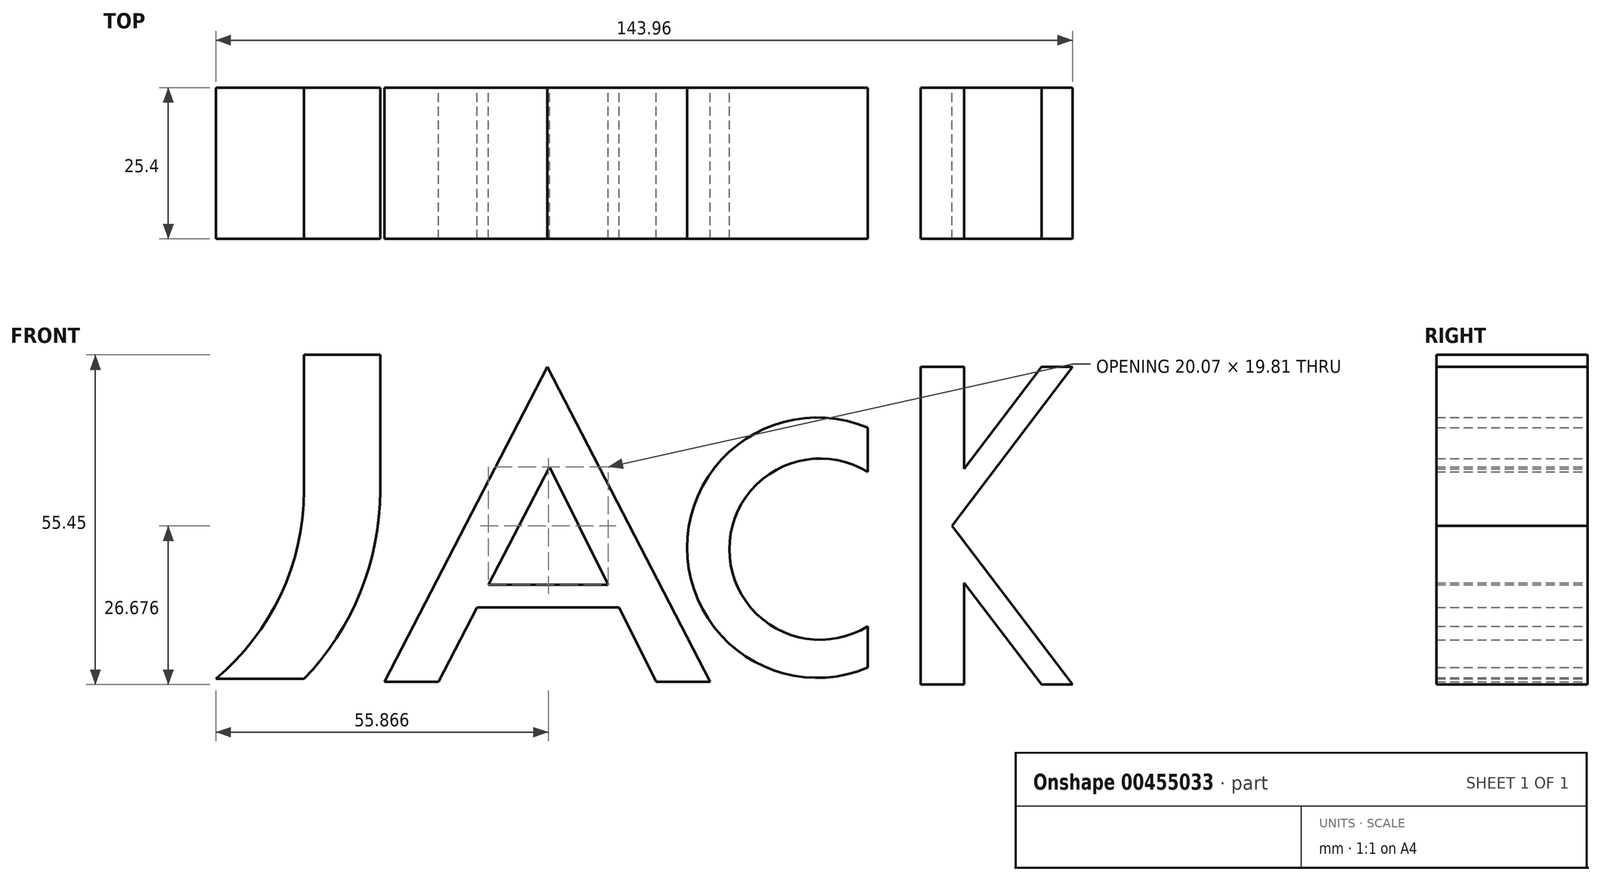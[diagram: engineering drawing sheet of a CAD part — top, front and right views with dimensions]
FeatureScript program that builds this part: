
annotation { "Feature Type Name" : "Feature", "Feature Type Description" : "" }
export const myFeature = defineFeature(function(context is Context, id is Id, definition is map)
    precondition{}
    {
        {
            var Q0;
            Q0=qCreatedBy(makeId("Front.planeOp"),FACE);
            var sketch = newSketch(context, id + "F0", { "sketchPlane" : qUnion([Q0])});
            skLineSegment(sketch, "E0", {"start": v(-52.69, 32.43) * mm, "end": v(-39.89, 32.43) * mm});
            skLineSegment(sketch, "E1", {"start": v(-39.89, 32.43) * mm, "end": v(-39.89, 9.58) * mm});
            skLineSegment(sketch, "E2", {"start": v(-39.89, 9.58) * mm, "end": v(-39.89, 32.43) * mm});
            skLineSegment(sketch, "E3", {"start": v(-52.69, 32.43) * mm, "end": v(-52.69, 9.58) * mm});
            skArc(sketch, "E4", {"start": v(-52.69, -22.05) * mm, "mid": v(-43.2, -7.48) * mm, "end": v(-39.89, 9.58) * mm});
            skPoint(sketch, "E4.startSnap0", {"position": v(-52.69, 21) * mm});
            skArc(sketch, "E5", {"start": v(-67.5, -22.05) * mm, "mid": v(-56.58, -7.88) * mm, "end": v(-52.69, 9.58) * mm});
            skLineSegment(sketch, "E6", {"start": v(-67.5, -22.05) * mm, "end": v(-52.69, -22.05) * mm});
            skLineSegment(sketch, "E7", {"start": v(-39.13, -22.55) * mm, "end": v(-11.76, 30.42) * mm});
            skLineSegment(sketch, "E8", {"start": v(-11.76, 30.42) * mm, "end": v(15.6, -22.55) * mm});
            skLineSegment(sketch, "E9", {"start": v(-39.13, -22.55) * mm, "end": v(-30.1, -22.55) * mm});
            skLineSegment(sketch, "E10", {"start": v(-30.1, -22.55) * mm, "end": v(-23.64, -10.06) * mm});
            skLineSegment(sketch, "E11", {"start": v(15.6, -22.55) * mm, "end": v(6.5, -22.55) * mm});
            skLineSegment(sketch, "E12", {"start": v(-11.44, 13.56) * mm, "end": v(-1.6, -6.25) * mm});
            skLineSegment(sketch, "E13", {"start": v(-23.64, -10.06) * mm, "end": v(0, -10.06) * mm});
            skLineSegment(sketch, "E14", {"start": v(0, -10.06) * mm, "end": v(-23.64, -10.06) * mm});
            skLineSegment(sketch, "E15", {"start": v(-1.6, -6.25) * mm, "end": v(-21.67, -6.25) * mm});
            skLineSegment(sketch, "E16.trimOffspring", {"start": v(-21.67, -6.25) * mm, "end": v(-11.44, 13.56) * mm});
            skLineSegment(sketch, "E17", {"start": v(0, -10.06) * mm, "end": v(0.3, -10.06) * mm});
            skLineSegment(sketch, "E18", {"start": v(0.3, -10.06) * mm, "end": v(0, -10.06) * mm});
            skLineSegment(sketch, "E19.trimOffspring", {"start": v(0.3, -10.06) * mm, "end": v(6.5, -22.55) * mm});
            skPoint(sketch, "E20.end.orphan", {"position": v(28.2, -22.55) * mm});
            skPoint(sketch, "E20.start.orphan", {"position": v(26.93, 30.42) * mm});
            skArc(sketch, "E21", {"start": v(42.04, 20.17) * mm, "mid": v(11.7, 0) * mm, "end": v(42.04, -20.17) * mm});
            skLineSegment(sketch, "E22", {"start": v(42.04, 20.17) * mm, "end": v(42.04, 12.72) * mm});
            skArc(sketch, "E23", {"start": v(42.04, 12.72) * mm, "mid": v(18.8, -0.25) * mm, "end": v(42.04, -13.22) * mm});
            skLineSegment(sketch, "E24.trimOffspring", {"start": v(42.04, -13.22) * mm, "end": v(42.04, -20.17) * mm});
            skLineSegment(sketch, "E25", {"start": v(50.97, 30.42) * mm, "end": v(50.97, -23.02) * mm});
            skLineSegment(sketch, "E26", {"start": v(50.97, -23.02) * mm, "end": v(50.97, 30.42) * mm});
            skLineSegment(sketch, "E27", {"start": v(50.97, 30.42) * mm, "end": v(58.24, 30.42) * mm});
            skLineSegment(sketch, "E28", {"start": v(58.24, -23.02) * mm, "end": v(58.24, -5.9) * mm});
            skLineSegment(sketch, "E29", {"start": v(50.97, -23.02) * mm, "end": v(58.24, -23.02) * mm});
            skLineSegment(sketch, "E30", {"start": v(58.24, 13.3) * mm, "end": v(71.24, 30.42) * mm});
            skLineSegment(sketch, "E31", {"start": v(71.24, 30.42) * mm, "end": v(58.24, 13.3) * mm});
            skLineSegment(sketch, "E32", {"start": v(58.24, -5.9) * mm, "end": v(71.24, -23.02) * mm});
            skLineSegment(sketch, "E33", {"start": v(71.24, -23.02) * mm, "end": v(58.24, -5.9) * mm});
            skLineSegment(sketch, "E34", {"start": v(56.2, 3.7) * mm, "end": v(76.46, 30.42) * mm});
            skPoint(sketch, "E34.startSnap0", {"position": v(58.24, 3.7) * mm});
            skLineSegment(sketch, "E35", {"start": v(76.46, 30.42) * mm, "end": v(71.24, 30.42) * mm});
            skLineSegment(sketch, "E36", {"start": v(56.2, 3.7) * mm, "end": v(76.46, -23.02) * mm});
            skLineSegment(sketch, "E37", {"start": v(71.24, -23.02) * mm, "end": v(76.46, -23.02) * mm});
            skLineSegment(sketch, "E38.trimOffspring", {"start": v(58.24, 13.3) * mm, "end": v(58.24, 30.42) * mm});
            skPoint(sketch, "E39.orphan", {"position": v(50.97, 3.7) * mm});
            skSolve(sketch);
        }
        {
            var Q0;
            Q0 = qSketchRegion(id + "F0", true);
            extrude(context, id + "F1", {"entities" : qUnion([Q0]), "depth" : 25.4 * mm});
        }
    });
